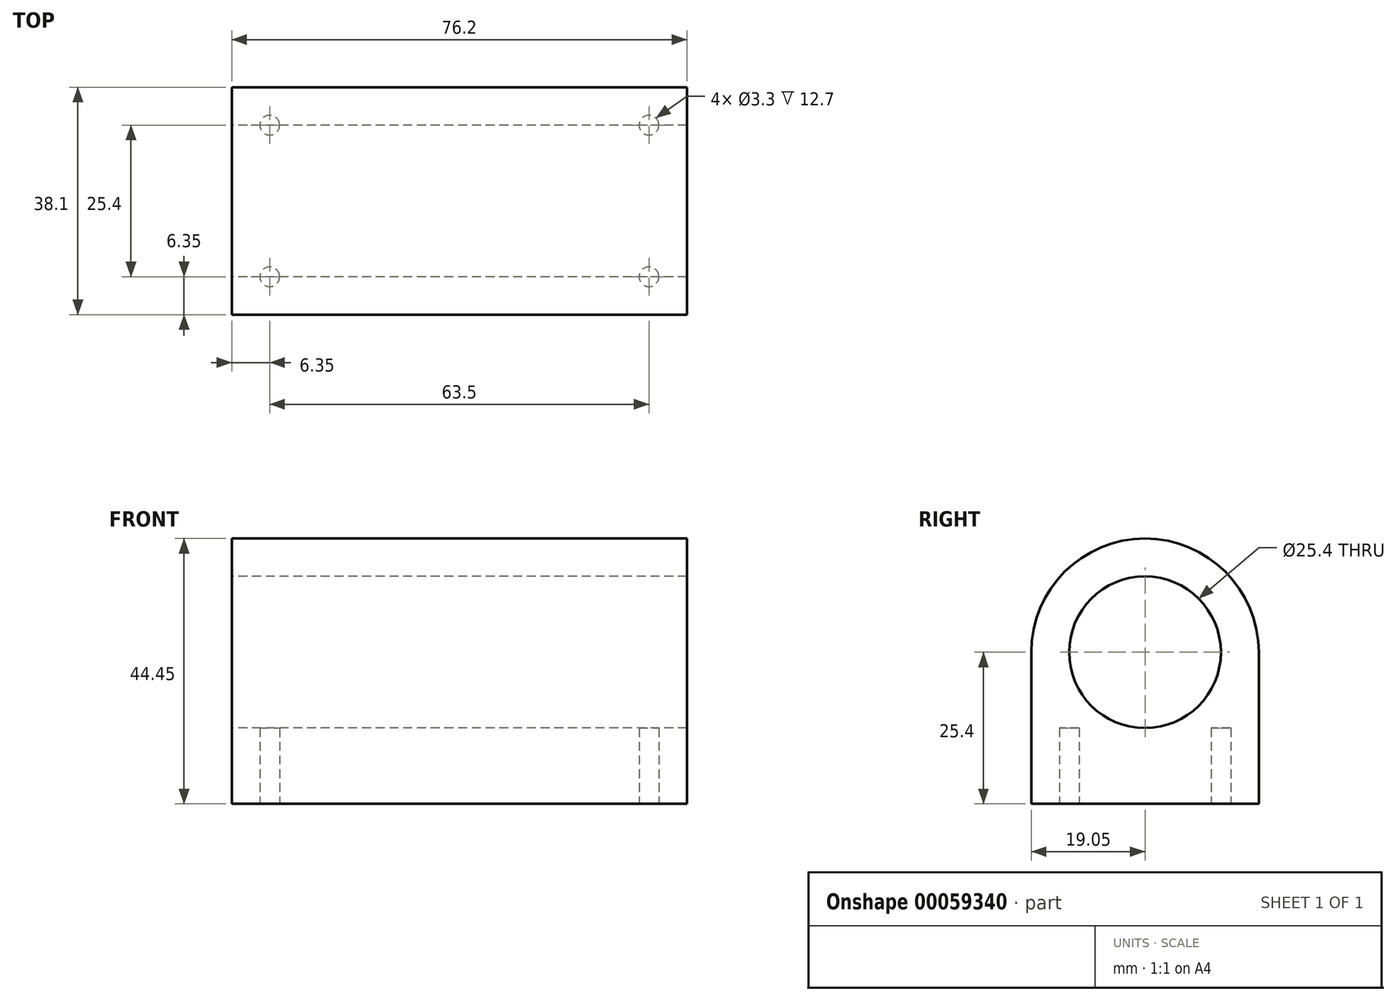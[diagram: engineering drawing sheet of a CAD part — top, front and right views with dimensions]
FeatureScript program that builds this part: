
annotation { "Feature Type Name" : "Feature", "Feature Type Description" : "" }
export const myFeature = defineFeature(function(context is Context, id is Id, definition is map)
    precondition{}
    {
        {
            var Q0;
            Q0=qCreatedBy(makeId("Right.planeOp"),FACE);
            var sketch = newSketch(context, id + "F0", { "sketchPlane" : qUnion([Q0])});
            skLineSegment(sketch, "E0.bottom", {"start": v(-19.05, 0) * mm, "end": v(19.05, 0) * mm});
            skLineSegment(sketch, "E0.top", {"start": v(-19.05, -25.4) * mm, "end": v(19.05, -25.4) * mm});
            skLineSegment(sketch, "E0.left", {"start": v(-19.05, 0) * mm, "end": v(-19.05, -25.4) * mm});
            skLineSegment(sketch, "E0.right", {"start": v(19.05, 0) * mm, "end": v(19.05, -25.4) * mm});
            skArc(sketch, "E1", {"start": v(19.05, 0) * mm, "mid": v(0, 19.05) * mm, "end": v(-19.05, 0) * mm});
            skCircle(sketch, "E2", {"center": v(0, 0) * mm, "radius": 12.7 * mm});
            skSolve(sketch);
        }
        {
            var Q0;
            Q0 = qSketchRegion(id + "F0", true);
            extrude(context, id + "F1", {"entities" : qUnion([Q0]), "depth" : 76.2 * mm});
        }
        {
            var Q0;
            Q0=makeQuery(id+"F1.opExtrude","SWEPT_FACE",FACE,{"disambiguationData":[OSD([sQuery(id+"F0.wireOp",EDGE,"E0.top")])]});
            var sketch = newSketch(context, id + "F2", { "sketchPlane" : qUnion([Q0])});
            skCircle(sketch, "E3", {"center": v(69.85, 12.7) * mm, "radius": 1.65 * mm});
            skCircle(sketch, "E4", {"center": v(69.85, -12.7) * mm, "radius": 1.65 * mm});
            skCircle(sketch, "E5", {"center": v(6.35, 12.7) * mm, "radius": 1.65 * mm});
            skCircle(sketch, "E6", {"center": v(6.35, -12.7) * mm, "radius": 1.65 * mm});
            skSolve(sketch);
        }
        {
            var Q0;
            Q0 = qSketchRegion(id + "F2", true);
            extrude(context, id + "F3", {"entities" : qUnion([Q0]), "operationType" : NewBodyOperationType.REMOVE, "oppositeDirection" : true, "depth" : 12.7 * mm});
        }
    });
